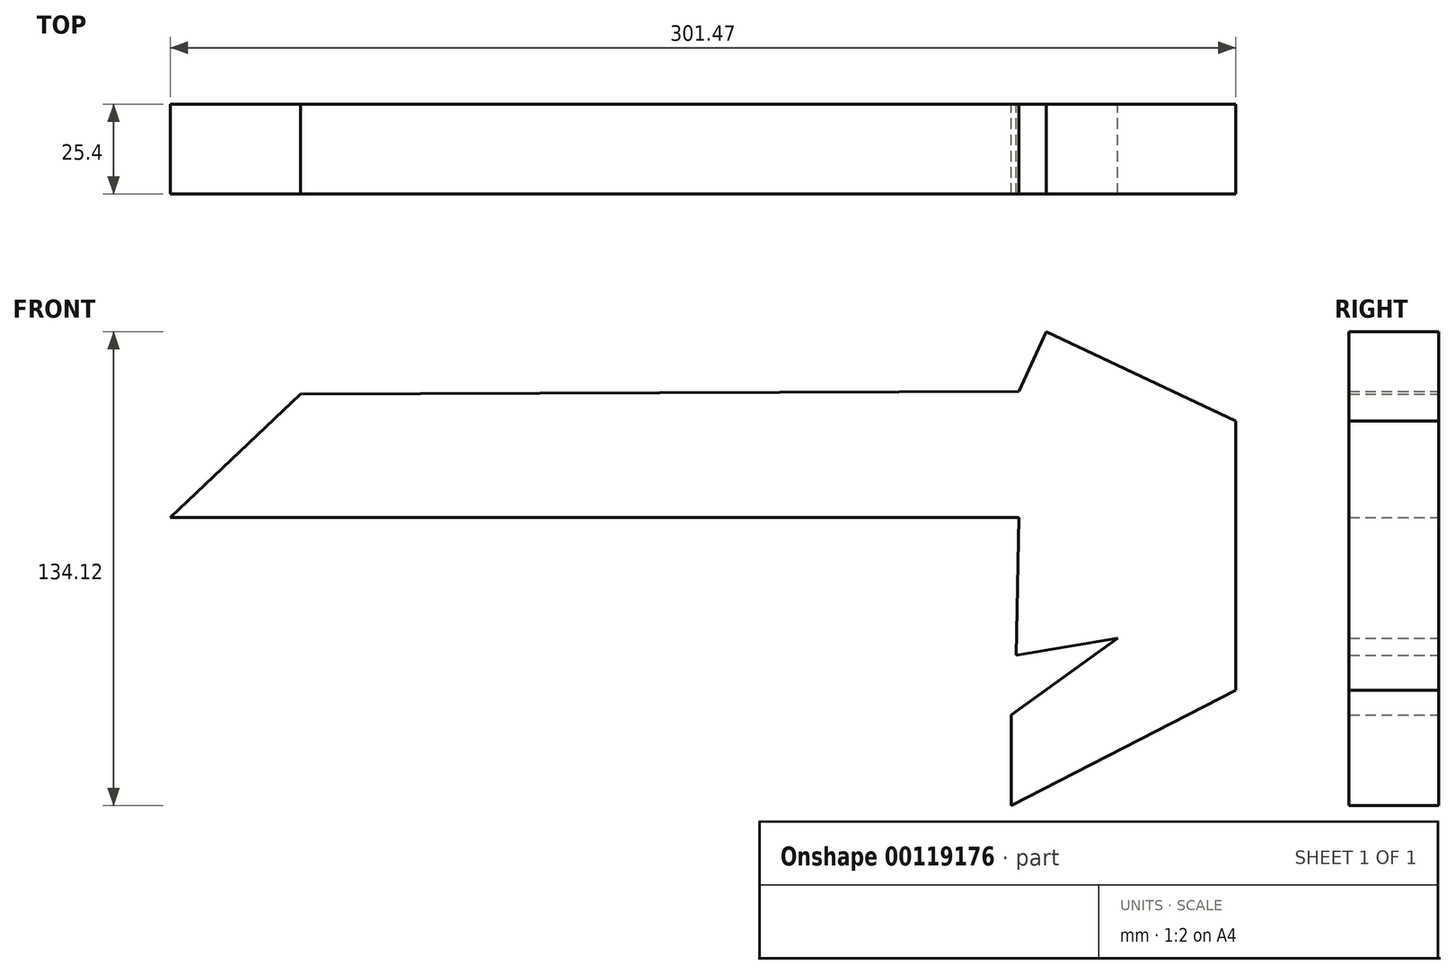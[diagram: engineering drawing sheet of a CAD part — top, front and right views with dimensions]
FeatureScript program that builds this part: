
annotation { "Feature Type Name" : "Feature", "Feature Type Description" : "" }
export const myFeature = defineFeature(function(context is Context, id is Id, definition is map)
    precondition{}
    {
        {
            var Q0;
            Q0=qCreatedBy(makeId("Front.planeOp"),FACE);
            var sketch = newSketch(context, id + "F0", { "sketchPlane" : qUnion([Q0])});
            skLineSegment(sketch, "E0", {"start": v(-102.71, 44.04) * mm, "end": v(-139.62, 9.13) * mm});
            skLineSegment(sketch, "E1", {"start": v(-139.62, 9.13) * mm, "end": v(100.48, 9.13) * mm});
            skLineSegment(sketch, "E2", {"start": v(100.48, 9.13) * mm, "end": v(100.48, 44.77) * mm});
            skLineSegment(sketch, "E3", {"start": v(100.48, 44.77) * mm, "end": v(-102.71, 44.04) * mm});
            skLineSegment(sketch, "E4", {"start": v(100.48, 44.77) * mm, "end": v(108.2, 61.68) * mm});
            skLineSegment(sketch, "E5", {"start": v(108.2, 61.68) * mm, "end": v(161.85, 36.46) * mm});
            skLineSegment(sketch, "E6", {"start": v(161.85, 36.46) * mm, "end": v(161.85, -39.74) * mm});
            skLineSegment(sketch, "E7", {"start": v(161.85, -39.74) * mm, "end": v(98.28, -72.44) * mm});
            skLineSegment(sketch, "E8", {"start": v(98.28, -72.44) * mm, "end": v(98.28, -46.72) * mm});
            skLineSegment(sketch, "E9", {"start": v(98.28, -46.72) * mm, "end": v(128.41, -25.04) * mm});
            skLineSegment(sketch, "E10", {"start": v(128.41, -25.04) * mm, "end": v(99.75, -29.82) * mm});
            skLineSegment(sketch, "E11", {"start": v(99.75, -29.82) * mm, "end": v(100.48, 9.13) * mm});
            skSolve(sketch);
        }
        {
            var Q0;
            Q0=makeQuery(id+"F0.imprint","IMPRINT",FACE,{"disambiguationData":[TD([[makeQuery(id+"F0.imprint","IMPRINT",EDGE,{"derivedFrom":sQuery(id+"F0.wireOp",EDGE,"E0")}),1.0]])]});
            var Q1;
            Q1=makeQuery(id+"F0.imprint","IMPRINT",FACE,{"disambiguationData":[TD([[makeQuery(id+"F0.imprint","IMPRINT",EDGE,{"derivedFrom":sQuery(id+"F0.wireOp",EDGE,"E2")}),-1.0]])]});
            extrude(context, id + "F1", {"entities" : qUnion([Q0, Q1]), "depth" : 25.4 * mm});
        }
    });
